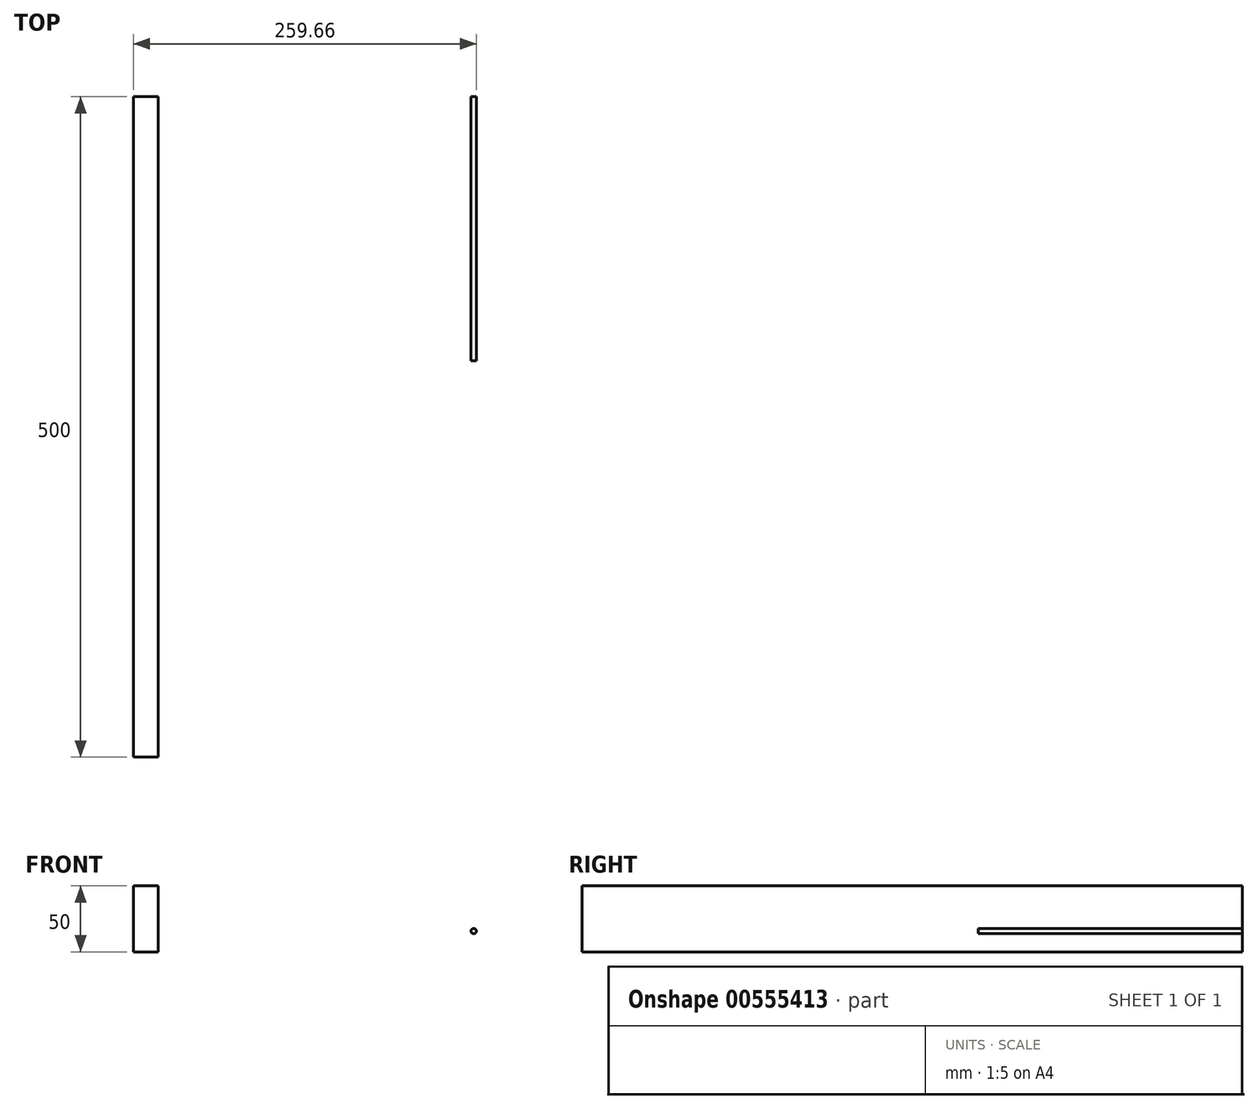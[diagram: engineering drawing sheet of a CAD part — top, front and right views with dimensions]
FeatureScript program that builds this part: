
annotation { "Feature Type Name" : "Feature", "Feature Type Description" : "" }
export const myFeature = defineFeature(function(context is Context, id is Id, definition is map)
    precondition{}
    {
        {
            var Q0;
            Q0=qCreatedBy(makeId("Front.planeOp"),FACE);
            var sketch = newSketch(context, id + "F0", { "sketchPlane" : qUnion([Q0])});
            skCircle(sketch, "E0", {"center": v(-12.73, 15.69) * mm, "radius": 2 * mm});
            skSolve(sketch);
        }
        {
            var Q0;
            Q0=makeQuery(id+"F0.imprint","IMPRINT",FACE,{"disambiguationData":[TD([[makeQuery(id+"F0.imprint","IMPRINT",EDGE,{"derivedFrom":sQuery(id+"F0.wireOp",EDGE,"E0")}),1.0]])]});
            extrude(context, id + "F1", {"entities" : qUnion([Q0]), "depth" : 200 * mm, "offsetDistance" : 25 * mm});
        }
        {
            var Q0;
            Q0=qCreatedBy(makeId("Front.planeOp"),FACE);
            var sketch = newSketch(context, id + "F2", { "sketchPlane" : qUnion([Q0])});
            skLineSegment(sketch, "E1", {"start": v(-270.39, 50) * mm, "end": v(-270.39, 0) * mm});
            skLineSegment(sketch, "E2", {"start": v(-270.39, 0) * mm, "end": v(-251.64, 0) * mm});
            skLineSegment(sketch, "E3", {"start": v(-251.64, 0) * mm, "end": v(-251.64, 50) * mm});
            skLineSegment(sketch, "E4", {"start": v(-251.64, 50) * mm, "end": v(-270.39, 50) * mm});
            skSolve(sketch);
        }
        {
            var Q0;
            Q0=makeQuery(id+"F2.imprint","IMPRINT",FACE,{"disambiguationData":[TD([[makeQuery(id+"F2.imprint","IMPRINT",EDGE,{"derivedFrom":sQuery(id+"F2.wireOp",EDGE,"E1")}),1.0]])]});
            extrude(context, id + "F3", {"entities" : qUnion([Q0]), "depth" : 500 * mm, "offsetDistance" : 25 * mm});
        }
    });
